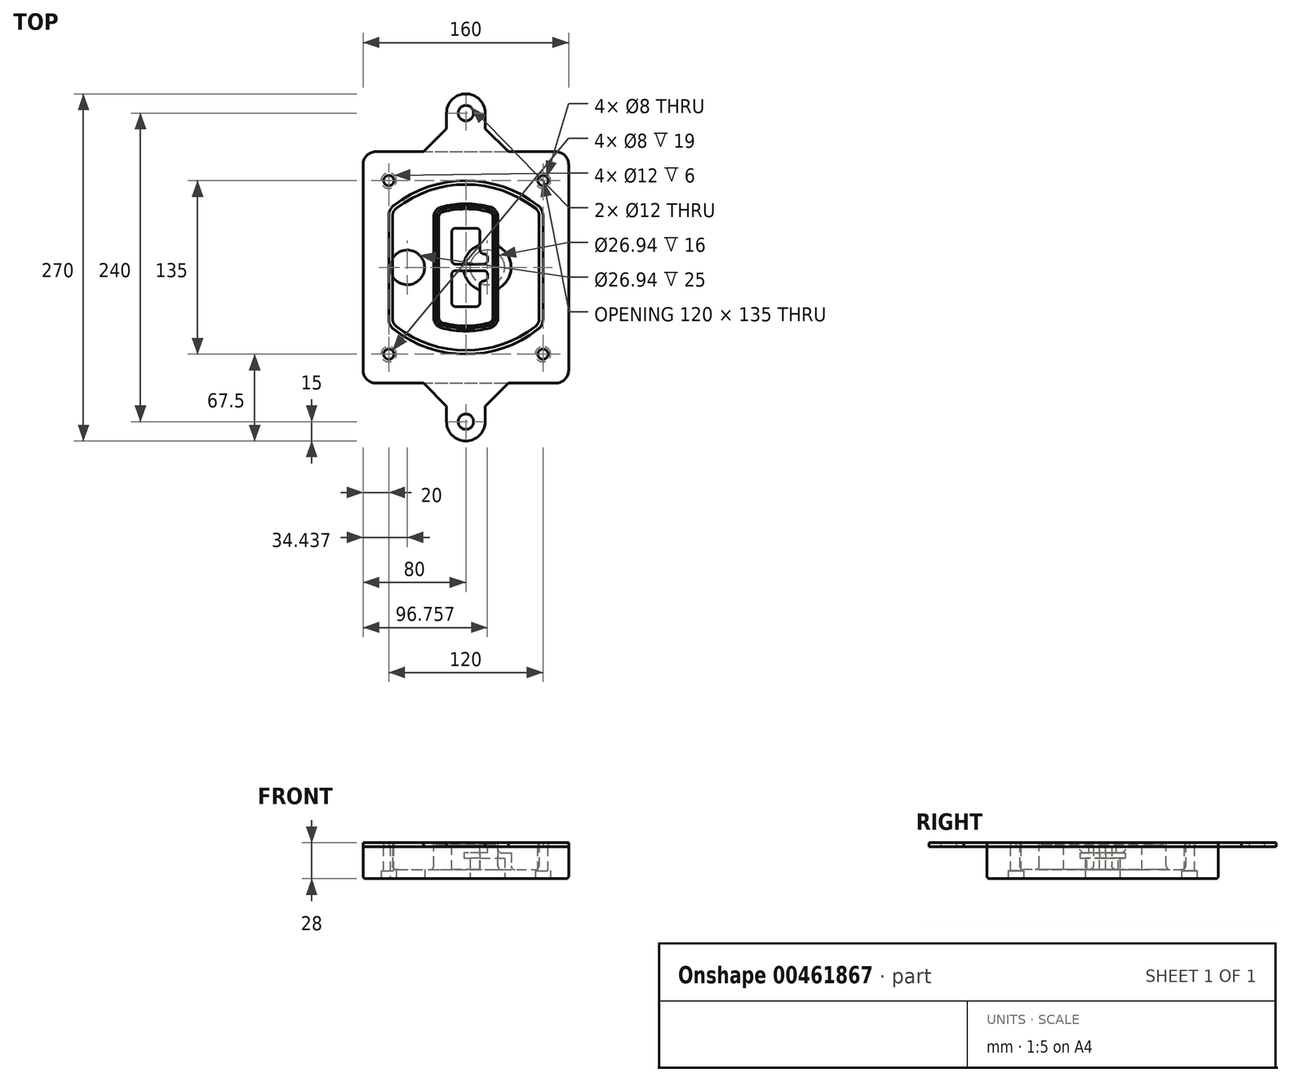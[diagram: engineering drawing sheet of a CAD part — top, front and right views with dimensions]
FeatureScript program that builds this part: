
annotation { "Feature Type Name" : "Feature", "Feature Type Description" : "" }
export const myFeature = defineFeature(function(context is Context, id is Id, definition is map)
    precondition{}
    {
        {
            var Q0;
            Q0=qCreatedBy(makeId("Top.planeOp"),FACE);
            var sketch = newSketch(context, id + "F0", { "sketchPlane" : qUnion([Q0])});
            skPoint(sketch, "E0.rect.middle", {"position": v(0, 0) * mm});
            skLineSegment(sketch, "E1.bottom", {"start": v(-70, -90) * mm, "end": v(70, -90) * mm});
            skLineSegment(sketch, "E1.top", {"start": v(-70, 90) * mm, "end": v(70, 90) * mm});
            skLineSegment(sketch, "E1.left", {"start": v(-80, -80) * mm, "end": v(-80, 80) * mm});
            skLineSegment(sketch, "E1.right", {"start": v(80, -80) * mm, "end": v(80, 80) * mm});
            skLineSegment(sketch, "E2", {"start": v(-80, 90) * mm, "end": v(80, -90) * mm, "construction": true});
            skLineSegment(sketch, "E3", {"start": v(80, 90) * mm, "end": v(-80, -90) * mm, "construction": true});
            skCircle(sketch, "E4", {"center": v(-60, 67.5) * mm, "radius": 4 * mm});
            skCircle(sketch, "E5", {"center": v(60, 67.5) * mm, "radius": 4 * mm});
            skCircle(sketch, "E6", {"center": v(60, -67.5) * mm, "radius": 4 * mm});
            skCircle(sketch, "E7", {"center": v(-60, -67.5) * mm, "radius": 4 * mm});
            skLineSegment(sketch, "E8", {"start": v(-60, 67.5) * mm, "end": v(60, 67.5) * mm, "construction": true});
            skLineSegment(sketch, "E9", {"start": v(60, 67.5) * mm, "end": v(60, -67.5) * mm, "construction": true});
            skLineSegment(sketch, "E10", {"start": v(60, -67.5) * mm, "end": v(-60, -67.5) * mm, "construction": true});
            skLineSegment(sketch, "E11", {"start": v(-60, -67.5) * mm, "end": v(-60, 67.5) * mm, "construction": true});
            skLineSegment(sketch, "E12", {"start": v(-60, 40.3) * mm, "end": v(-60, -40.3) * mm});
            skLineSegment(sketch, "E13", {"start": v(60, 40.3) * mm, "end": v(60, -40.3) * mm});
            skArc(sketch, "E14", {"start": v(56.15, 48.18) * mm, "mid": v(0, 67.5) * mm, "end": v(-56.15, 48.18) * mm});
            skArc(sketch, "E15", {"start": v(-56.15, -48.18) * mm, "mid": v(0, -67.5) * mm, "end": v(56.15, -48.18) * mm});
            skLineSegment(sketch, "E16", {"start": v(-60, 0) * mm, "end": v(60, 0) * mm, "construction": true});
            skPoint(sketch, "E17.visualSharp", {"position": v(-60, -45) * mm});
            skArc(sketch, "E17.filletArc", {"start": v(-60, -40.3) * mm, "mid": v(-58.99, -44.68) * mm, "end": v(-56.15, -48.18) * mm});
            skPoint(sketch, "E18.visualSharp", {"position": v(-60, 45) * mm});
            skArc(sketch, "E18.filletArc", {"start": v(-56.15, 48.18) * mm, "mid": v(-58.99, 44.68) * mm, "end": v(-60, 40.3) * mm});
            skPoint(sketch, "E19.visualSharp", {"position": v(60, 45) * mm});
            skArc(sketch, "E19.filletArc", {"start": v(60, 40.3) * mm, "mid": v(58.99, 44.68) * mm, "end": v(56.15, 48.18) * mm});
            skPoint(sketch, "E20.visualSharp", {"position": v(60, -45) * mm});
            skArc(sketch, "E20.filletArc", {"start": v(56.15, -48.18) * mm, "mid": v(58.99, -44.68) * mm, "end": v(60, -40.3) * mm});
            skPoint(sketch, "E21.visualSharp", {"position": v(-80, 90) * mm});
            skArc(sketch, "E21.filletArc", {"start": v(-70, 90) * mm, "mid": v(-77.07, 87.07) * mm, "end": v(-80, 80) * mm});
            skPoint(sketch, "E22.visualSharp", {"position": v(80, 90) * mm});
            skArc(sketch, "E22.filletArc", {"start": v(80, 80) * mm, "mid": v(77.07, 87.07) * mm, "end": v(70, 90) * mm});
            skPoint(sketch, "E23.visualSharp", {"position": v(80, -90) * mm});
            skArc(sketch, "E23.filletArc", {"start": v(70, -90) * mm, "mid": v(77.07, -87.07) * mm, "end": v(80, -80) * mm});
            skPoint(sketch, "E24.visualSharp", {"position": v(-80, -90) * mm});
            skArc(sketch, "E24.filletArc", {"start": v(-80, -80) * mm, "mid": v(-77.07, -87.07) * mm, "end": v(-70, -90) * mm});
            skArc(sketch, "E25.0", {"start": v(57, 40.3) * mm, "mid": v(56.3, 43.36) * mm, "end": v(54.3, 45.81) * mm});
            skLineSegment(sketch, "E25.1", {"start": v(57, 40.3) * mm, "end": v(57, -40.3) * mm});
            skArc(sketch, "E25.2", {"start": v(54.3, -45.81) * mm, "mid": v(56.3, -43.36) * mm, "end": v(57, -40.3) * mm});
            skArc(sketch, "E25.3", {"start": v(-54.3, -45.81) * mm, "mid": v(0, -64.5) * mm, "end": v(54.3, -45.81) * mm});
            skArc(sketch, "E25.4", {"start": v(-57, -40.3) * mm, "mid": v(-56.3, -43.36) * mm, "end": v(-54.3, -45.81) * mm});
            skArc(sketch, "E25.5", {"start": v(54.3, 45.81) * mm, "mid": v(0, 64.5) * mm, "end": v(-54.3, 45.81) * mm});
            skLineSegment(sketch, "E25.6", {"start": v(-57, 40.3) * mm, "end": v(-57, -40.3) * mm});
            skArc(sketch, "E25.7", {"start": v(-54.3, 45.81) * mm, "mid": v(-56.3, 43.36) * mm, "end": v(-57, 40.3) * mm});
            skArc(sketch, "E26.0", {"start": v(-58.62, 51.33) * mm, "mid": v(-62.58, 46.43) * mm, "end": v(-64, 40.3) * mm});
            skArc(sketch, "E26.1", {"start": v(58.62, 51.33) * mm, "mid": v(0, 71.5) * mm, "end": v(-58.62, 51.33) * mm});
            skArc(sketch, "E26.2", {"start": v(64, 40.3) * mm, "mid": v(62.58, 46.43) * mm, "end": v(58.62, 51.33) * mm});
            skLineSegment(sketch, "E26.3", {"start": v(64, 40.3) * mm, "end": v(64, -40.3) * mm});
            skArc(sketch, "E26.4", {"start": v(58.62, -51.33) * mm, "mid": v(62.58, -46.43) * mm, "end": v(64, -40.3) * mm});
            skLineSegment(sketch, "E26.5", {"start": v(-64, 40.3) * mm, "end": v(-64, -40.3) * mm});
            skArc(sketch, "E26.6", {"start": v(-58.62, -51.33) * mm, "mid": v(0, -71.5) * mm, "end": v(58.62, -51.33) * mm});
            skArc(sketch, "E26.7", {"start": v(-64, -40.3) * mm, "mid": v(-62.58, -46.43) * mm, "end": v(-58.62, -51.33) * mm});
            skSolve(sketch);
        }
        {
            var Q0;
            Q0=makeQuery(id+"F0.imprint","IMPRINT",FACE,{"disambiguationData":[TD([[makeQuery(id+"F0.imprint","IMPRINT",EDGE,{"derivedFrom":sQuery(id+"F0.wireOp",EDGE,"E1.bottom")}),1.0]])]});
            var Q1;
            Q1=makeQuery(id+"F0.imprint","IMPRINT",FACE,{"disambiguationData":[TD([[makeQuery(id+"F0.imprint","IMPRINT",EDGE,{"derivedFrom":sQuery(id+"F0.wireOp",EDGE,"E12")}),1.0]])]});
            var Q2;
            Q2=makeQuery(id+"F0.imprint","IMPRINT",FACE,{"disambiguationData":[TD([[makeQuery(id+"F0.imprint","IMPRINT",EDGE,{"derivedFrom":sQuery(id+"F0.wireOp",EDGE,"E25.0")}),1.0]])]});
            var Q3;
            Q3=makeQuery(id+"F0.imprint","IMPRINT",FACE,{"disambiguationData":[TD([[makeQuery(id+"F0.imprint","IMPRINT",EDGE,{"derivedFrom":sQuery(id+"F0.wireOp",EDGE,"E12")}),-1.0]])]});
            extrude(context, id + "F1", {"entities" : qUnion([Q0, Q1, Q2, Q3]), "oppositeDirection" : true, "depth" : 25 * mm});
        }
        {
            var Q0;
            Q0=makeQuery(id+"F0.imprint","IMPRINT",FACE,{"disambiguationData":[TD([[makeQuery(id+"F0.imprint","IMPRINT",EDGE,{"derivedFrom":sQuery(id+"F0.wireOp",EDGE,"E12")}),1.0]])]});
            extrude(context, id + "F2", {"entities" : qUnion([Q0]), "operationType" : NewBodyOperationType.ADD, "depth" : 3 * mm});
        }
        {
            var Q0;
            Q0=makeQuery(id+"F0.imprint","IMPRINT",FACE,{"disambiguationData":[TD([[makeQuery(id+"F0.imprint","IMPRINT",EDGE,{"derivedFrom":sQuery(id+"F0.wireOp",EDGE,"E25.0")}),1.0]])]});
            extrude(context, id + "F3", {"entities" : qUnion([Q0]), "operationType" : NewBodyOperationType.REMOVE, "oppositeDirection" : true, "depth" : 18 * mm});
        }
        {
            var Q0;
            Q0=makeQuery(id+"F2.opExtrude","CAP_FACE",FACE,{"disambiguationData":[OSD([sQuery(id+"F0.wireOp",EDGE,"E12"),sQuery(id+"F0.wireOp",EDGE,"E13"),sQuery(id+"F0.wireOp",EDGE,"E14"),sQuery(id+"F0.wireOp",EDGE,"E15"),sQuery(id+"F0.wireOp",EDGE,"E17.filletArc"),sQuery(id+"F0.wireOp",EDGE,"E18.filletArc"),sQuery(id+"F0.wireOp",EDGE,"E19.filletArc"),sQuery(id+"F0.wireOp",EDGE,"E20.filletArc"),sQuery(id+"F0.wireOp",EDGE,"E25.0"),sQuery(id+"F0.wireOp",EDGE,"E25.1"),sQuery(id+"F0.wireOp",EDGE,"E25.2"),sQuery(id+"F0.wireOp",EDGE,"E25.3"),sQuery(id+"F0.wireOp",EDGE,"E25.4"),sQuery(id+"F0.wireOp",EDGE,"E25.5"),sQuery(id+"F0.wireOp",EDGE,"E25.6"),sQuery(id+"F0.wireOp",EDGE,"E25.7")])],"isStart":false});
            var sketch = newSketch(context, id + "F4", { "sketchPlane" : qUnion([Q0])});
            skArc(sketch, "E27.0", {"start": v(-19.08, -46.97) * mm, "mid": v(0, -49.5) * mm, "end": v(19.08, -46.97) * mm});
            skArc(sketch, "E28.0", {"start": v(19.08, 46.97) * mm, "mid": v(0, 49.5) * mm, "end": v(-19.08, 46.97) * mm});
            skLineSegment(sketch, "E29", {"start": v(-25, 39.25) * mm, "end": v(-25, -39.25) * mm});
            skLineSegment(sketch, "E30", {"start": v(25, 39.25) * mm, "end": v(25, -39.25) * mm});
            skLineSegment(sketch, "E31", {"start": v(-25, 45.1) * mm, "end": v(25, 45.1) * mm, "construction": true});
            skLineSegment(sketch, "E32", {"start": v(-25, -45.1) * mm, "end": v(25, -45.1) * mm, "construction": true});
            skPoint(sketch, "E33.visualSharp", {"position": v(-25, 45.1) * mm});
            skArc(sketch, "E33.filletArc", {"start": v(-19.08, 46.97) * mm, "mid": v(-23.35, 44.11) * mm, "end": v(-25, 39.25) * mm});
            skPoint(sketch, "E34.visualSharp", {"position": v(25, 45.1) * mm});
            skArc(sketch, "E34.filletArc", {"start": v(25, 39.25) * mm, "mid": v(23.35, 44.11) * mm, "end": v(19.08, 46.97) * mm});
            skPoint(sketch, "E35.visualSharp", {"position": v(25, -45.1) * mm});
            skArc(sketch, "E35.filletArc", {"start": v(19.08, -46.97) * mm, "mid": v(23.35, -44.11) * mm, "end": v(25, -39.25) * mm});
            skPoint(sketch, "E36.visualSharp", {"position": v(-25, -45.1) * mm});
            skArc(sketch, "E36.filletArc", {"start": v(-25, -39.25) * mm, "mid": v(-23.35, -44.11) * mm, "end": v(-19.08, -46.97) * mm});
            skArc(sketch, "E37.0", {"start": v(54.3, 45.81) * mm, "mid": v(0, 64.5) * mm, "end": v(-54.3, 45.81) * mm});
            skArc(sketch, "E37.1", {"start": v(-54.3, 45.81) * mm, "mid": v(-56.3, 43.36) * mm, "end": v(-57, 40.3) * mm});
            skLineSegment(sketch, "E37.2", {"start": v(-57, 40.3) * mm, "end": v(-57, -40.3) * mm});
            skArc(sketch, "E37.3", {"start": v(-57, -40.3) * mm, "mid": v(-56.3, -43.36) * mm, "end": v(-54.3, -45.81) * mm});
            skArc(sketch, "E37.4", {"start": v(-54.3, -45.81) * mm, "mid": v(0, -64.5) * mm, "end": v(54.3, -45.81) * mm});
            skArc(sketch, "E37.5", {"start": v(54.3, -45.81) * mm, "mid": v(56.3, -43.36) * mm, "end": v(57, -40.3) * mm});
            skLineSegment(sketch, "E37.6", {"start": v(57, 40.3) * mm, "end": v(57, -40.3) * mm});
            skArc(sketch, "E37.7", {"start": v(57, 40.3) * mm, "mid": v(56.3, 43.36) * mm, "end": v(54.3, 45.81) * mm});
            skLineSegment(sketch, "E38.0", {"start": v(23, 39.25) * mm, "end": v(23, -39.25) * mm});
            skArc(sketch, "E38.1", {"start": v(18.56, -45.04) * mm, "mid": v(21.76, -42.9) * mm, "end": v(23, -39.25) * mm});
            skArc(sketch, "E38.2", {"start": v(-18.56, -45.04) * mm, "mid": v(0, -47.5) * mm, "end": v(18.56, -45.04) * mm});
            skArc(sketch, "E38.3", {"start": v(-23, -39.25) * mm, "mid": v(-21.76, -42.9) * mm, "end": v(-18.56, -45.04) * mm});
            skLineSegment(sketch, "E38.4", {"start": v(-23, 39.25) * mm, "end": v(-23, -39.25) * mm});
            skArc(sketch, "E38.5", {"start": v(23, 39.25) * mm, "mid": v(21.76, 42.9) * mm, "end": v(18.56, 45.04) * mm});
            skArc(sketch, "E38.6", {"start": v(-18.56, 45.04) * mm, "mid": v(-21.76, 42.9) * mm, "end": v(-23, 39.25) * mm});
            skArc(sketch, "E38.7", {"start": v(18.56, 45.04) * mm, "mid": v(0, 47.5) * mm, "end": v(-18.56, 45.04) * mm});
            skArc(sketch, "E39.0", {"start": v(21, 39.25) * mm, "mid": v(20.18, 41.68) * mm, "end": v(18.04, 43.1) * mm});
            skLineSegment(sketch, "E39.1", {"start": v(21, 39.25) * mm, "end": v(21, -39.25) * mm});
            skArc(sketch, "E39.2", {"start": v(18.04, -43.1) * mm, "mid": v(20.18, -41.68) * mm, "end": v(21, -39.25) * mm});
            skArc(sketch, "E39.3", {"start": v(-18.04, -43.1) * mm, "mid": v(0, -45.5) * mm, "end": v(18.04, -43.1) * mm});
            skArc(sketch, "E39.4", {"start": v(-21, -39.25) * mm, "mid": v(-20.18, -41.68) * mm, "end": v(-18.04, -43.1) * mm});
            skArc(sketch, "E39.5", {"start": v(18.04, 43.1) * mm, "mid": v(0, 45.5) * mm, "end": v(-18.04, 43.1) * mm});
            skLineSegment(sketch, "E39.6", {"start": v(-21, 39.25) * mm, "end": v(-21, -39.25) * mm});
            skArc(sketch, "E39.7", {"start": v(-18.04, 43.1) * mm, "mid": v(-20.18, 41.68) * mm, "end": v(-21, 39.25) * mm});
            skLineSegment(sketch, "E40", {"start": v(-25, 0) * mm, "end": v(25, 0) * mm, "construction": true});
            skLineSegment(sketch, "E41", {"start": v(-11, 5.5) * mm, "end": v(-11, 27.5) * mm});
            skLineSegment(sketch, "E42", {"start": v(-8, 30.5) * mm, "end": v(8, 30.5) * mm});
            skLineSegment(sketch, "E43", {"start": v(11, 27.5) * mm, "end": v(11, 13.5) * mm});
            skLineSegment(sketch, "E44", {"start": v(14, 10.5) * mm, "end": v(14, 10.5) * mm});
            skLineSegment(sketch, "E45", {"start": v(17, 7.5) * mm, "end": v(17, 5.5) * mm});
            skLineSegment(sketch, "E46", {"start": v(14, 2.5) * mm, "end": v(-8, 2.5) * mm});
            skPoint(sketch, "E47.visualSharp", {"position": v(-11, 30.5) * mm});
            skArc(sketch, "E47.filletArc", {"start": v(-8, 30.5) * mm, "mid": v(-10.12, 29.62) * mm, "end": v(-11, 27.5) * mm});
            skPoint(sketch, "E48.visualSharp", {"position": v(11, 30.5) * mm});
            skArc(sketch, "E48.filletArc", {"start": v(11, 27.5) * mm, "mid": v(10.12, 29.62) * mm, "end": v(8, 30.5) * mm});
            skPoint(sketch, "E49.visualSharp", {"position": v(11, 10.5) * mm});
            skArc(sketch, "E49.filletArc", {"start": v(11, 13.5) * mm, "mid": v(11.88, 11.38) * mm, "end": v(14, 10.5) * mm});
            skPoint(sketch, "E50.visualSharp", {"position": v(17, 10.5) * mm});
            skArc(sketch, "E50.filletArc", {"start": v(17, 7.5) * mm, "mid": v(16.12, 9.62) * mm, "end": v(14, 10.5) * mm});
            skPoint(sketch, "E51.visualSharp", {"position": v(17, 2.5) * mm});
            skArc(sketch, "E51.filletArc", {"start": v(14, 2.5) * mm, "mid": v(16.12, 3.38) * mm, "end": v(17, 5.5) * mm});
            skPoint(sketch, "E52.visualSharp", {"position": v(-11, 2.5) * mm});
            skArc(sketch, "E52.filletArc", {"start": v(-11, 5.5) * mm, "mid": v(-10.12, 3.38) * mm, "end": v(-8, 2.5) * mm});
            skLineSegment(sketch, "E53.0.MirrorCS", {"start": v(14, -2.5) * mm, "end": v(-8, -2.5) * mm});
            skArc(sketch, "E54.0.MirrorCS", {"start": v(-11, -5.5) * mm, "mid": v(-10.12, -3.38) * mm, "end": v(-8, -2.5) * mm});
            skLineSegment(sketch, "E55.0.MirrorCS", {"start": v(-11, -5.5) * mm, "end": v(-11, -27.5) * mm});
            skArc(sketch, "E56.0.MirrorCS", {"start": v(-8, -30.5) * mm, "mid": v(-10.12, -29.62) * mm, "end": v(-11, -27.5) * mm});
            skLineSegment(sketch, "E57.0.MirrorCS", {"start": v(-8, -30.5) * mm, "end": v(8, -30.5) * mm});
            skArc(sketch, "E58.0.MirrorCS", {"start": v(11, -27.5) * mm, "mid": v(10.12, -29.62) * mm, "end": v(8, -30.5) * mm});
            skLineSegment(sketch, "E59.0.MirrorCS", {"start": v(11, -27.5) * mm, "end": v(11, -13.5) * mm});
            skArc(sketch, "E60.0.MirrorCS", {"start": v(11, -13.5) * mm, "mid": v(11.88, -11.38) * mm, "end": v(14, -10.5) * mm});
            skArc(sketch, "E61.0.MirrorCS", {"start": v(17, -7.5) * mm, "mid": v(16.12, -9.62) * mm, "end": v(14, -10.5) * mm});
            skLineSegment(sketch, "E62.0.MirrorCS", {"start": v(17, -7.5) * mm, "end": v(17, -5.5) * mm});
            skArc(sketch, "E63.0.MirrorCS", {"start": v(14, -2.5) * mm, "mid": v(16.12, -3.38) * mm, "end": v(17, -5.5) * mm});
            skSolve(sketch);
        }
        {
            var Q0;
            Q0=makeQuery(id+"F4.imprint","IMPRINT",FACE,{"disambiguationData":[TD([[makeQuery(id+"F4.imprint","IMPRINT",EDGE,{"derivedFrom":sQuery(id+"F4.wireOp",EDGE,"E27.0")}),1.0]])]});
            var Q1;
            Q1=makeQuery(id+"F4.imprint","IMPRINT",FACE,{"disambiguationData":[TD([[makeQuery(id+"F4.imprint","IMPRINT",EDGE,{"derivedFrom":sQuery(id+"F4.wireOp",EDGE,"E38.0")}),-1.0]])]});
            var Q2;
            Q2=makeQuery(id+"F4.imprint","IMPRINT",FACE,{"disambiguationData":[TD([[makeQuery(id+"F4.imprint","IMPRINT",EDGE,{"derivedFrom":sQuery(id+"F4.wireOp",EDGE,"E39.0")}),1.0]])]});
            extrude(context, id + "F5", {"entities" : qUnion([Q0, Q1, Q2]), "operationType" : NewBodyOperationType.ADD, "endBound" : BoundingType.UP_TO_NEXT, "oppositeDirection" : true, "depth" : 25 * mm});
        }
        {
            var Q0;
            Q0=makeQuery(id+"F4.imprint","IMPRINT",FACE,{"disambiguationData":[TD([[makeQuery(id+"F4.imprint","IMPRINT",EDGE,{"derivedFrom":sQuery(id+"F4.wireOp",EDGE,"E38.0")}),-1.0]])]});
            extrude(context, id + "F6", {"entities" : qUnion([Q0]), "operationType" : NewBodyOperationType.REMOVE, "oppositeDirection" : true, "depth" : 2 * mm});
        }
        {
            var Q0;
            Q0=makeQuery(id+"F1.opExtrude","CAP_FACE",FACE,{"disambiguationData":[OSD([sQuery(id+"F0.wireOp",EDGE,"E1.bottom"),sQuery(id+"F0.wireOp",EDGE,"E1.top"),sQuery(id+"F0.wireOp",EDGE,"E1.left"),sQuery(id+"F0.wireOp",EDGE,"E1.right"),sQuery(id+"F0.wireOp",EDGE,"E4"),sQuery(id+"F0.wireOp",EDGE,"E5"),sQuery(id+"F0.wireOp",EDGE,"E6"),sQuery(id+"F0.wireOp",EDGE,"E7"),sQuery(id+"F0.wireOp",EDGE,"E21.filletArc"),sQuery(id+"F0.wireOp",EDGE,"E22.filletArc"),sQuery(id+"F0.wireOp",EDGE,"E23.filletArc"),sQuery(id+"F0.wireOp",EDGE,"E24.filletArc")])],"isStart":false});
            var sketch = newSketch(context, id + "F7", { "sketchPlane" : qUnion([Q0])});
            skCircle(sketch, "E64", {"center": v(16.76, 0) * mm, "radius": 13.47 * mm});
            skCircle(sketch, "E65", {"center": v(-45.56, 0) * mm, "radius": 13.47 * mm});
            skLineSegment(sketch, "E66", {"start": v(80, 0) * mm, "end": v(-80, 0) * mm});
            skCircle(sketch, "E67", {"center": v(16.76, 0) * mm, "radius": 18.47 * mm});
            skCircle(sketch, "E68", {"center": v(60, -67.5) * mm, "radius": 6 * mm});
            skCircle(sketch, "E69", {"center": v(-60, -67.5) * mm, "radius": 6 * mm});
            skCircle(sketch, "E70", {"center": v(-60, 67.5) * mm, "radius": 6 * mm});
            skCircle(sketch, "E71", {"center": v(60, 67.5) * mm, "radius": 6 * mm});
            skSolve(sketch);
        }
        {
            var Q0;
            {var subQ1=sQuery(id+"F7.wireOp",EDGE,"E66");var subQ4=sQuery(id+"F7.wireOp",EDGE,"E64");var subQ6=makeQuery(id+"F7.imprint","INTERSECT",VERTEX,{"disambiguationData":[OD(0.0)],"derivedFrom":[subQ4,subQ1]});Q0=makeQuery(id+"F7.imprint","IMPRINT",FACE,{"disambiguationData":[TD([[makeQuery(id+"F7.imprint","IMPRINT",EDGE,{"disambiguationData":[TD([[subQ6,-1.0]])],"derivedFrom":subQ4}),-1.0]])]});}
            var Q1;
            {var subQ0=sQuery(id+"F7.wireOp",EDGE,"E66");var subQ1=sQuery(id+"F7.wireOp",EDGE,"E64");var subQ3=makeQuery(id+"F7.imprint","INTERSECT",VERTEX,{"disambiguationData":[OD(0.0)],"derivedFrom":[subQ1,subQ0]});Q1=makeQuery(id+"F7.imprint","IMPRINT",FACE,{"disambiguationData":[TD([[makeQuery(id+"F7.imprint","IMPRINT",EDGE,{"disambiguationData":[TD([[subQ3,-1.0]])],"derivedFrom":subQ1}),1.0]])]});}
            var Q2;
            {var subQ0=sQuery(id+"F7.wireOp",EDGE,"E66");var subQ1=sQuery(id+"F7.wireOp",EDGE,"E64");var subQ3=makeQuery(id+"F7.imprint","INTERSECT",VERTEX,{"disambiguationData":[OD(0.0)],"derivedFrom":[subQ1,subQ0]});Q2=makeQuery(id+"F7.imprint","IMPRINT",FACE,{"disambiguationData":[TD([[makeQuery(id+"F7.imprint","IMPRINT",EDGE,{"disambiguationData":[TD([[subQ3,1.0]])],"derivedFrom":subQ1}),1.0]])]});}
            var Q3;
            {var subQ1=sQuery(id+"F7.wireOp",EDGE,"E66");var subQ4=sQuery(id+"F7.wireOp",EDGE,"E64");var subQ6=makeQuery(id+"F7.imprint","INTERSECT",VERTEX,{"disambiguationData":[OD(0.0)],"derivedFrom":[subQ4,subQ1]});Q3=makeQuery(id+"F7.imprint","IMPRINT",FACE,{"disambiguationData":[TD([[makeQuery(id+"F7.imprint","IMPRINT",EDGE,{"disambiguationData":[TD([[subQ6,1.0]])],"derivedFrom":subQ4}),-1.0]])]});}
            extrude(context, id + "F8", {"entities" : qUnion([Q0, Q1, Q2, Q3]), "operationType" : NewBodyOperationType.ADD, "oppositeDirection" : true, "depth" : 20 * mm});
        }
        {
            var Q0;
            {var subQ0=sQuery(id+"F7.wireOp",EDGE,"E66");var subQ1=sQuery(id+"F7.wireOp",EDGE,"E64");var subQ3=makeQuery(id+"F7.imprint","INTERSECT",VERTEX,{"disambiguationData":[OD(0.0)],"derivedFrom":[subQ1,subQ0]});Q0=makeQuery(id+"F7.imprint","IMPRINT",FACE,{"disambiguationData":[TD([[makeQuery(id+"F7.imprint","IMPRINT",EDGE,{"disambiguationData":[TD([[subQ3,-1.0]])],"derivedFrom":subQ1}),1.0]])]});}
            var Q1;
            {var subQ0=sQuery(id+"F7.wireOp",EDGE,"E66");var subQ1=sQuery(id+"F7.wireOp",EDGE,"E64");var subQ3=makeQuery(id+"F7.imprint","INTERSECT",VERTEX,{"disambiguationData":[OD(0.0)],"derivedFrom":[subQ1,subQ0]});Q1=makeQuery(id+"F7.imprint","IMPRINT",FACE,{"disambiguationData":[TD([[makeQuery(id+"F7.imprint","IMPRINT",EDGE,{"disambiguationData":[TD([[subQ3,1.0]])],"derivedFrom":subQ1}),1.0]])]});}
            extrude(context, id + "F9", {"entities" : qUnion([Q0, Q1]), "operationType" : NewBodyOperationType.REMOVE, "oppositeDirection" : true, "depth" : 16 * mm});
        }
        {
            var Q0;
            {var subQ0=sQuery(id+"F7.wireOp",EDGE,"E66");var subQ1=sQuery(id+"F7.wireOp",EDGE,"E65");var subQ3=makeQuery(id+"F7.imprint","INTERSECT",VERTEX,{"disambiguationData":[OD(0.0)],"derivedFrom":[subQ1,subQ0]});Q0=makeQuery(id+"F7.imprint","IMPRINT",FACE,{"disambiguationData":[TD([[makeQuery(id+"F7.imprint","IMPRINT",EDGE,{"disambiguationData":[TD([[subQ3,-1.0]])],"derivedFrom":subQ1}),1.0]])]});}
            var Q1;
            {var subQ0=sQuery(id+"F7.wireOp",EDGE,"E66");var subQ1=sQuery(id+"F7.wireOp",EDGE,"E65");var subQ3=makeQuery(id+"F7.imprint","INTERSECT",VERTEX,{"disambiguationData":[OD(0.0)],"derivedFrom":[subQ1,subQ0]});Q1=makeQuery(id+"F7.imprint","IMPRINT",FACE,{"disambiguationData":[TD([[makeQuery(id+"F7.imprint","IMPRINT",EDGE,{"disambiguationData":[TD([[subQ3,1.0]])],"derivedFrom":subQ1}),1.0]])]});}
            extrude(context, id + "F10", {"entities" : qUnion([Q0, Q1]), "operationType" : NewBodyOperationType.REMOVE, "oppositeDirection" : true, "depth" : 25 * mm});
        }
        {
            var Q0;
            Q0=makeQuery(id+"F7.imprint","IMPRINT",FACE,{"disambiguationData":[TD([[makeQuery(id+"F7.imprint","IMPRINT",EDGE,{"derivedFrom":sQuery(id+"F7.wireOp",EDGE,"E68")}),1.0]])]});
            var Q1;
            Q1=makeQuery(id+"F7.imprint","IMPRINT",FACE,{"disambiguationData":[TD([[makeQuery(id+"F7.imprint","IMPRINT",EDGE,{"derivedFrom":makeQuery(id+"F1.opExtrude","CAP_EDGE",EDGE,{"disambiguationData":[OSD([sQuery(id+"F0.wireOp",EDGE,"E5")])],"isStart":false})}),-1.0]])]});
            var Q2;
            Q2=makeQuery(id+"F7.imprint","IMPRINT",FACE,{"disambiguationData":[TD([[makeQuery(id+"F7.imprint","IMPRINT",EDGE,{"derivedFrom":sQuery(id+"F7.wireOp",EDGE,"E69")}),1.0]])]});
            var Q3;
            Q3=makeQuery(id+"F7.imprint","IMPRINT",FACE,{"disambiguationData":[TD([[makeQuery(id+"F7.imprint","IMPRINT",EDGE,{"derivedFrom":makeQuery(id+"F1.opExtrude","CAP_EDGE",EDGE,{"disambiguationData":[OSD([sQuery(id+"F0.wireOp",EDGE,"E4")])],"isStart":false})}),-1.0]])]});
            var Q4;
            Q4=makeQuery(id+"F7.imprint","IMPRINT",FACE,{"disambiguationData":[TD([[makeQuery(id+"F7.imprint","IMPRINT",EDGE,{"derivedFrom":sQuery(id+"F7.wireOp",EDGE,"E70")}),1.0]])]});
            var Q5;
            Q5=makeQuery(id+"F7.imprint","IMPRINT",FACE,{"disambiguationData":[TD([[makeQuery(id+"F7.imprint","IMPRINT",EDGE,{"derivedFrom":makeQuery(id+"F1.opExtrude","CAP_EDGE",EDGE,{"disambiguationData":[OSD([sQuery(id+"F0.wireOp",EDGE,"E7")])],"isStart":false})}),-1.0]])]});
            var Q6;
            Q6=makeQuery(id+"F7.imprint","IMPRINT",FACE,{"disambiguationData":[TD([[makeQuery(id+"F7.imprint","IMPRINT",EDGE,{"derivedFrom":sQuery(id+"F7.wireOp",EDGE,"E71")}),1.0]])]});
            var Q7;
            Q7=makeQuery(id+"F7.imprint","IMPRINT",FACE,{"disambiguationData":[TD([[makeQuery(id+"F7.imprint","IMPRINT",EDGE,{"derivedFrom":makeQuery(id+"F1.opExtrude","CAP_EDGE",EDGE,{"disambiguationData":[OSD([sQuery(id+"F0.wireOp",EDGE,"E6")])],"isStart":false})}),-1.0]])]});
            extrude(context, id + "F11", {"entities" : qUnion([Q0, Q1, Q2, Q3, Q4, Q5, Q6, Q7]), "operationType" : NewBodyOperationType.REMOVE, "oppositeDirection" : true, "depth" : 6 * mm});
        }
        {
            var Q0;
            Q0=makeQuery(id+"F9.boolean.opBoolean","COPY",FACE,{"derivedFrom":makeQuery(id+"F9.opExtrude","CAP_FACE",FACE,{"disambiguationData":[OSD([sQuery(id+"F7.wireOp",EDGE,"E64")])],"isStart":false})});
            var sketch = newSketch(context, id + "F12", { "sketchPlane" : qUnion([Q0])});
            skArc(sketch, "E72.0", {"start": v(11, 17.55) * mm, "mid": v(2.57, 11.82) * mm, "end": v(-1.54, 2.5) * mm});
            skArc(sketch, "E72.1", {"start": v(-1.54, -2.5) * mm, "mid": v(2.57, -11.82) * mm, "end": v(11, -17.55) * mm});
            skLineSegment(sketch, "E73", {"start": v(-1.54, -2.5) * mm, "end": v(14, -2.5) * mm});
            skLineSegment(sketch, "E74.0", {"start": v(14, 2.5) * mm, "end": v(-1.54, 2.5) * mm});
            skArc(sketch, "E74.1", {"start": v(14, 2.5) * mm, "mid": v(16.12, 3.38) * mm, "end": v(17, 5.5) * mm});
            skLineSegment(sketch, "E74.2", {"start": v(17, 7.5) * mm, "end": v(17, 5.5) * mm});
            skArc(sketch, "E74.3", {"start": v(17, 7.5) * mm, "mid": v(16.12, 9.62) * mm, "end": v(14, 10.5) * mm});
            skArc(sketch, "E74.4", {"start": v(11, 13.5) * mm, "mid": v(11.88, 11.38) * mm, "end": v(14, 10.5) * mm});
            skLineSegment(sketch, "E74.5", {"start": v(11, 17.55) * mm, "end": v(11, 13.5) * mm});
            skLineSegment(sketch, "E74.7", {"start": v(14, -2.5) * mm, "end": v(-1.54, -2.5) * mm});
            skArc(sketch, "E74.8", {"start": v(14, -2.5) * mm, "mid": v(16.12, -3.38) * mm, "end": v(17, -5.5) * mm});
            skLineSegment(sketch, "E74.9", {"start": v(17, -7.5) * mm, "end": v(17, -5.5) * mm});
            skArc(sketch, "E74.10", {"start": v(17, -7.5) * mm, "mid": v(16.12, -9.62) * mm, "end": v(14, -10.5) * mm});
            skArc(sketch, "E74.11", {"start": v(11, -13.5) * mm, "mid": v(11.88, -11.38) * mm, "end": v(14, -10.5) * mm});
            skLineSegment(sketch, "E74.12", {"start": v(11, -17.55) * mm, "end": v(11, -13.5) * mm});
            skPoint(sketch, "E75.orphan", {"position": v(11, -27.5) * mm});
            skPoint(sketch, "E76.orphan", {"position": v(-8, -2.5) * mm});
            skPoint(sketch, "E77.orphan", {"position": v(-8, 2.5) * mm});
            skPoint(sketch, "E78.orphan", {"position": v(11, 27.5) * mm});
            skSolve(sketch);
        }
        {
            var Q0;
            {var subQ7=sQuery(id+"F12.wireOp",EDGE,"E72.0");var subQ14=sQuery(id+"F12.wireOp",EDGE,"E72.1");var subQ16=sQuery(id+"F12.wireOp",EDGE,"E74.1");var subQ18=sQuery(id+"F12.wireOp",EDGE,"E74.8");Q0=qUnion([makeQuery(id+"F12.imprint","IMPRINT",FACE,{"disambiguationData":[TD([[makeQuery(id+"F12.imprint","IMPRINT",EDGE,{"derivedFrom":subQ7}),1.0]])]}),makeQuery(id+"F12.imprint","IMPRINT",FACE,{"disambiguationData":[TD([[makeQuery(id+"F12.imprint","IMPRINT",EDGE,{"derivedFrom":subQ14}),1.0]])]}),makeQuery(id+"F12.imprint","IMPRINT",FACE,{"disambiguationData":[TD([[makeQuery(id+"F12.imprint","IMPRINT",EDGE,{"derivedFrom":subQ16}),1.0]])]}),makeQuery(id+"F12.imprint","IMPRINT",FACE,{"disambiguationData":[TD([[makeQuery(id+"F12.imprint","IMPRINT",EDGE,{"derivedFrom":subQ18}),-1.0]])]})]);}
            var Q1;
            Q1=makeQuery(id+"F5.boolean.opBoolean","SPLIT",FACE,{"disambiguationData":[TD([makeQuery(id+"F5.opExtrude","SWEPT_FACE",FACE,{"disambiguationData":[OSD([sQuery(id+"F4.wireOp",EDGE,"E41")])]})])],"derivedFrom":makeQuery(id+"F3.boolean.opBoolean","COPY",FACE,{"derivedFrom":makeQuery(id+"F3.opExtrude","CAP_FACE",FACE,{"disambiguationData":[OSD([sQuery(id+"F0.wireOp",EDGE,"E25.0"),sQuery(id+"F0.wireOp",EDGE,"E25.1"),sQuery(id+"F0.wireOp",EDGE,"E25.2"),sQuery(id+"F0.wireOp",EDGE,"E25.3"),sQuery(id+"F0.wireOp",EDGE,"E25.4"),sQuery(id+"F0.wireOp",EDGE,"E25.5"),sQuery(id+"F0.wireOp",EDGE,"E25.6"),sQuery(id+"F0.wireOp",EDGE,"E25.7")])],"isStart":false})})});
            extrude(context, id + "F13", {"entities" : qUnion([Q0]), "operationType" : NewBodyOperationType.REMOVE, "endBound" : BoundingType.UP_TO_SURFACE, "endBoundEntityFace" : qUnion([Q1]), "depth" : 25 * mm});
        }
        {
            var Q0;
            Q0=makeQuery(id+"F3.boolean.opBoolean","COPY",EDGE,{"derivedFrom":makeQuery(id+"F3.opExtrude","CAP_EDGE",EDGE,{"disambiguationData":[OSD([sQuery(id+"F0.wireOp",EDGE,"E25.6")])],"isStart":false})});
            var Q1;
            Q1=makeQuery(id+"F8.boolean.opBoolean","INTERSECT",EDGE,{"derivedFrom":[makeQuery(id+"F5.opExtrude","SWEPT_FACE",FACE,{"disambiguationData":[OSD([sQuery(id+"F4.wireOp",EDGE,"E30")])]}),makeQuery(id+"F8.opExtrude","CAP_FACE",FACE,{"disambiguationData":[OSD([sQuery(id+"F7.wireOp",EDGE,"E67")])],"isStart":false})]});
            var Q2;
            Q2=makeQuery(id+"F8.boolean.opBoolean","INTERSECT",EDGE,{"disambiguationData":[OD(1.0)],"derivedFrom":[makeQuery(id+"F5.opExtrude","SWEPT_FACE",FACE,{"disambiguationData":[OSD([sQuery(id+"F4.wireOp",EDGE,"E30")])]}),makeQuery(id+"F8.opExtrude","SWEPT_FACE",FACE,{"disambiguationData":[OSD([sQuery(id+"F7.wireOp",EDGE,"E67")])]})]});
            var Q3;
            {var subQ0=sQuery(id+"F4.wireOp",EDGE,"E30");Q3=makeQuery(id+"F8.boolean.opBoolean","SPLIT",EDGE,{"disambiguationData":[TD([makeQuery(id+"F5.opExtrude","SWEPT_FACE",FACE,{"disambiguationData":[OSD([sQuery(id+"F4.wireOp",EDGE,"E35.filletArc")])]})])],"derivedFrom":makeQuery(id+"F5.opExtrude","CAP_EDGE",EDGE,{"disambiguationData":[OSD([subQ0])],"isStart":false})});}
            var Q4;
            {var subQ0=sQuery(id+"F0.wireOp",EDGE,"E25.7");var subQ1=sQuery(id+"F0.wireOp",EDGE,"E25.1");var subQ2=sQuery(id+"F0.wireOp",EDGE,"E25.6");var subQ3=sQuery(id+"F0.wireOp",EDGE,"E25.5");var subQ4=sQuery(id+"F0.wireOp",EDGE,"E25.4");var subQ5=sQuery(id+"F0.wireOp",EDGE,"E25.0");var subQ6=sQuery(id+"F0.wireOp",EDGE,"E25.2");var subQ7=sQuery(id+"F0.wireOp",EDGE,"E25.3");Q4=makeQuery(id+"F8.boolean.opBoolean","INTERSECT",EDGE,{"derivedFrom":[makeQuery(id+"F5.boolean.opBoolean","SPLIT",FACE,{"disambiguationData":[TD([makeQuery(id+"F2.opExtrude","SWEPT_FACE",FACE,{"disambiguationData":[OSD([subQ5])]})])],"derivedFrom":makeQuery(id+"F3.boolean.opBoolean","COPY",FACE,{"derivedFrom":makeQuery(id+"F3.opExtrude","CAP_FACE",FACE,{"disambiguationData":[OSD([subQ5,subQ1,subQ6,subQ7,subQ4,subQ3,subQ2,subQ0])],"isStart":false})})}),makeQuery(id+"F8.opExtrude","SWEPT_FACE",FACE,{"disambiguationData":[OSD([sQuery(id+"F7.wireOp",EDGE,"E67")])]})]});}
            var Q5;
            Q5=makeQuery(id+"F8.boolean.opBoolean","INTERSECT",EDGE,{"disambiguationData":[OD(0.0)],"derivedFrom":[makeQuery(id+"F5.opExtrude","SWEPT_FACE",FACE,{"disambiguationData":[OSD([sQuery(id+"F4.wireOp",EDGE,"E30")])]}),makeQuery(id+"F8.opExtrude","SWEPT_FACE",FACE,{"disambiguationData":[OSD([sQuery(id+"F7.wireOp",EDGE,"E67")])]})]});
            fillet(context, id + "F14", {"entities" : qUnion([Q0, Q1, Q2, Q3, Q4, Q5]), "radius" : 3 * mm, "tangentPropagation" : true, "allowEdgeOverflow" : false});
        }
        {
            var Q0;
            Q0=makeQuery(id+"F1.opExtrude","CAP_EDGE",EDGE,{"disambiguationData":[OSD([sQuery(id+"F0.wireOp",EDGE,"E1.bottom")])],"isStart":false});
            fillet(context, id + "F15", {"entities" : qUnion([Q0]), "radius" : 2 * mm, "tangentPropagation" : true, "allowEdgeOverflow" : false});
        }
        {
            var Q0;
            {var subQ0=sQuery(id+"F0.wireOp",EDGE,"E21.filletArc");var subQ1=sQuery(id+"F0.wireOp",EDGE,"E7");var subQ2=sQuery(id+"F0.wireOp",EDGE,"E6");var subQ3=sQuery(id+"F0.wireOp",EDGE,"E5");var subQ4=sQuery(id+"F0.wireOp",EDGE,"E4");var subQ5=sQuery(id+"F0.wireOp",EDGE,"E22.filletArc");var subQ6=sQuery(id+"F0.wireOp",EDGE,"E1.bottom");var subQ7=sQuery(id+"F0.wireOp",EDGE,"E1.right");var subQ8=sQuery(id+"F0.wireOp",EDGE,"E1.top");var subQ9=sQuery(id+"F0.wireOp",EDGE,"E1.left");var subQ10=sQuery(id+"F0.wireOp",EDGE,"E23.filletArc");var subQ11=sQuery(id+"F0.wireOp",EDGE,"E24.filletArc");Q0=makeQuery(id+"F2.boolean.opBoolean","SPLIT",FACE,{"disambiguationData":[TD([makeQuery(id+"F1.opExtrude","SWEPT_FACE",FACE,{"disambiguationData":[OSD([subQ6])]})])],"derivedFrom":makeQuery(id+"F1.opExtrude","CAP_FACE",FACE,{"disambiguationData":[OSD([subQ6,subQ8,subQ9,subQ7,subQ4,subQ3,subQ2,subQ1,subQ0,subQ5,subQ10,subQ11])],"isStart":true})});}
            var sketch = newSketch(context, id + "F16", { "sketchPlane" : qUnion([Q0])});
            skLineSegment(sketch, "E79", {"start": v(0, 90) * mm, "end": v(0, 120) * mm, "construction": true});
            skCircle(sketch, "E80", {"center": v(0, 120) * mm, "radius": 6 * mm});
            skArc(sketch, "E81", {"start": v(15, 120) * mm, "mid": v(0, 135) * mm, "end": v(-15, 120) * mm});
            skLineSegment(sketch, "E82", {"start": v(15, 120) * mm, "end": v(15, 108) * mm});
            skLineSegment(sketch, "E83", {"start": v(-15, 120) * mm, "end": v(-15, 108) * mm});
            skLineSegment(sketch, "E84", {"start": v(15, 108) * mm, "end": v(33, 90) * mm});
            skLineSegment(sketch, "E85", {"start": v(-15, 108) * mm, "end": v(-33, 90) * mm});
            skLineSegment(sketch, "E86", {"start": v(-80, 0) * mm, "end": v(80, 0) * mm, "construction": true});
            skLineSegment(sketch, "E87.MirrorCS", {"start": v(-15, -120) * mm, "end": v(-15, -108) * mm});
            skLineSegment(sketch, "E88.MirrorCS", {"start": v(15, -120) * mm, "end": v(15, -108) * mm});
            skLineSegment(sketch, "E89.MirrorCS", {"start": v(0, -90) * mm, "end": v(0, -120) * mm, "construction": true});
            skCircle(sketch, "E90.MirrorC", {"center": v(0, -120) * mm, "radius": 6 * mm});
            skLineSegment(sketch, "E91.MirrorCS", {"start": v(-15, -108) * mm, "end": v(-33, -90) * mm});
            skLineSegment(sketch, "E92.MirrorCS", {"start": v(15, -108) * mm, "end": v(33, -90) * mm});
            skArc(sketch, "E93.MirrorCS", {"start": v(15, -120) * mm, "mid": v(0, -135) * mm, "end": v(-15, -120) * mm});
            skSolve(sketch);
        }
        {
            var Q0;
            Q0=makeQuery(id+"F16.imprint","IMPRINT",FACE,{"disambiguationData":[TD([[makeQuery(id+"F16.imprint","IMPRINT",EDGE,{"derivedFrom":sQuery(id+"F16.wireOp",EDGE,"E80")}),-1.0]])]});
            var Q1;
            Q1=makeQuery(id+"F16.imprint","IMPRINT",FACE,{"disambiguationData":[TD([[makeQuery(id+"F16.imprint","IMPRINT",EDGE,{"derivedFrom":makeQuery(id+"F1.opExtrude","CAP_EDGE",EDGE,{"disambiguationData":[OSD([sQuery(id+"F0.wireOp",EDGE,"E1.left")])],"isStart":true})}),-1.0]])]});
            var Q2;
            Q2=makeQuery(id+"F16.imprint","IMPRINT",FACE,{"disambiguationData":[TD([[makeQuery(id+"F16.imprint","IMPRINT",EDGE,{"derivedFrom":sQuery(id+"F16.wireOp",EDGE,"E87.MirrorCS")}),-1.0]])]});
            var Q3;
            Q3=makeQuery(id+"F2.opExtrude","CAP_FACE",FACE,{"disambiguationData":[OSD([sQuery(id+"F0.wireOp",EDGE,"E12"),sQuery(id+"F0.wireOp",EDGE,"E13"),sQuery(id+"F0.wireOp",EDGE,"E14"),sQuery(id+"F0.wireOp",EDGE,"E15"),sQuery(id+"F0.wireOp",EDGE,"E17.filletArc"),sQuery(id+"F0.wireOp",EDGE,"E18.filletArc"),sQuery(id+"F0.wireOp",EDGE,"E19.filletArc"),sQuery(id+"F0.wireOp",EDGE,"E20.filletArc"),sQuery(id+"F0.wireOp",EDGE,"E25.0"),sQuery(id+"F0.wireOp",EDGE,"E25.1"),sQuery(id+"F0.wireOp",EDGE,"E25.2"),sQuery(id+"F0.wireOp",EDGE,"E25.3"),sQuery(id+"F0.wireOp",EDGE,"E25.4"),sQuery(id+"F0.wireOp",EDGE,"E25.5"),sQuery(id+"F0.wireOp",EDGE,"E25.6"),sQuery(id+"F0.wireOp",EDGE,"E25.7")])],"isStart":false});
            extrude(context, id + "F17", {"entities" : qUnion([Q0, Q1, Q2]), "endBound" : BoundingType.UP_TO_SURFACE, "endBoundEntityFace" : qUnion([Q3]), "depth" : 25 * mm});
        }
    });
